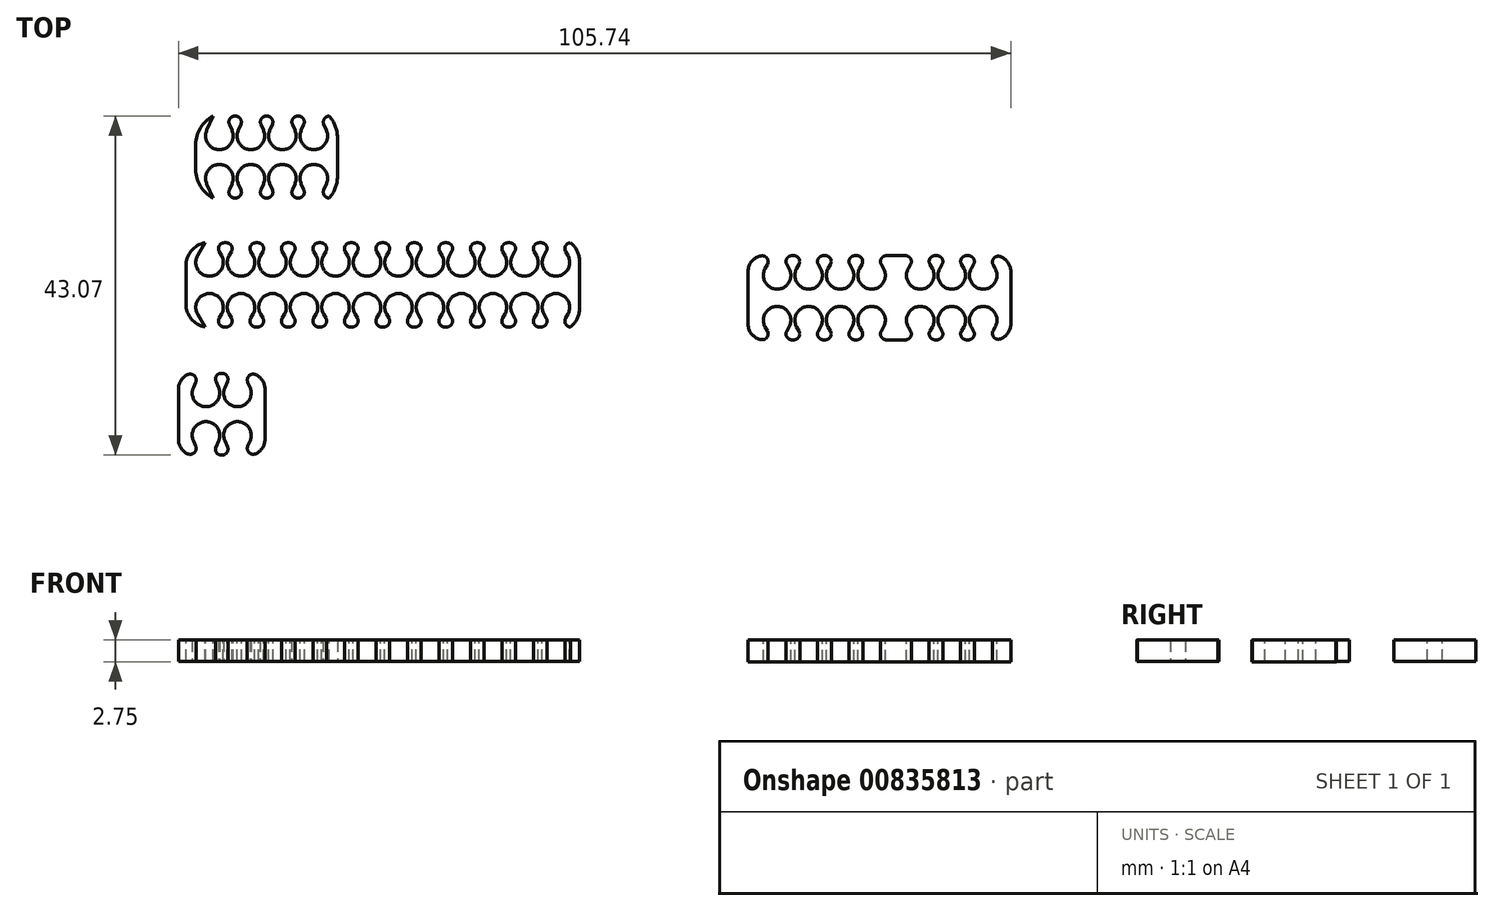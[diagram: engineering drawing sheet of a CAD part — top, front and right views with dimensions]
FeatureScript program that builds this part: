
annotation { "Feature Type Name" : "Feature", "Feature Type Description" : "" }
export const myFeature = defineFeature(function(context is Context, id is Id, definition is map)
    precondition{}
    {
        {
            var Q0;
            Q0=qCreatedBy(makeId("Top.planeOp"),FACE);
            var sketch = newSketch(context, id + "F0", { "sketchPlane" : qUnion([Q0])});
            skLineSegment(sketch, "E0.bottom", {"start": v(-25, 10.7) * mm, "end": v(25, 10.7) * mm});
            skLineSegment(sketch, "E0.top", {"start": v(-25, 0) * mm, "end": v(25, 0) * mm});
            skLineSegment(sketch, "E0.left", {"start": v(-25, 10.7) * mm, "end": v(-25, 0) * mm});
            skLineSegment(sketch, "E0.right", {"start": v(25, 10.7) * mm, "end": v(25, 0) * mm});
            skSolve(sketch);
        }
        {
            var Q0;
            Q0=makeQuery(id+"F0.imprint","IMPRINT",FACE,{"disambiguationData":[TD([[makeQuery(id+"F0.imprint","IMPRINT",EDGE,{"derivedFrom":sQuery(id+"F0.wireOp",EDGE,"E0.bottom")}),-1.0]])]});
            extrude(context, id + "F1", {"entities" : qUnion([Q0]), "depth" : 2.7 * mm});
        }
        {
            var Q0;
            Q0=makeQuery(id+"F1.opExtrude","CAP_FACE",FACE,{"disambiguationData":[OSD([sQuery(id+"F0.wireOp",EDGE,"E0.bottom"),sQuery(id+"F0.wireOp",EDGE,"E0.top"),sQuery(id+"F0.wireOp",EDGE,"E0.left"),sQuery(id+"F0.wireOp",EDGE,"E0.right")])],"isStart":false});
            var sketch = newSketch(context, id + "F2", { "sketchPlane" : qUnion([Q0])});
            skArc(sketch, "E1", {"start": v(-23.52, 9.07) * mm, "mid": v(-22, 6.45) * mm, "end": v(-20.48, 9.07) * mm});
            skArc(sketch, "E2", {"start": v(-19.52, 9.07) * mm, "mid": v(-18, 6.45) * mm, "end": v(-16.48, 9.07) * mm});
            skArc(sketch, "E3", {"start": v(-15.52, 9.07) * mm, "mid": v(-14, 6.45) * mm, "end": v(-12.48, 9.07) * mm});
            skArc(sketch, "E4", {"start": v(-11.52, 9.07) * mm, "mid": v(-10, 6.45) * mm, "end": v(-8.48, 9.07) * mm});
            skArc(sketch, "E5", {"start": v(-7.52, 9.07) * mm, "mid": v(-6, 6.45) * mm, "end": v(-4.48, 9.07) * mm});
            skArc(sketch, "E6", {"start": v(-3.52, 9.07) * mm, "mid": v(-2, 6.45) * mm, "end": v(-0.48, 9.07) * mm});
            skLineSegment(sketch, "E7", {"start": v(-19.52, 9.07) * mm, "end": v(-18.59, 10.7) * mm});
            skLineSegment(sketch, "E8", {"start": v(-16.48, 9.07) * mm, "end": v(-17.41, 10.7) * mm});
            skLineSegment(sketch, "E9", {"start": v(-15.52, 9.07) * mm, "end": v(-14.59, 10.7) * mm});
            skLineSegment(sketch, "E10", {"start": v(-12.48, 9.07) * mm, "end": v(-13.41, 10.7) * mm});
            skLineSegment(sketch, "E11", {"start": v(-11.52, 9.07) * mm, "end": v(-10.59, 10.7) * mm});
            skLineSegment(sketch, "E12", {"start": v(-8.48, 9.07) * mm, "end": v(-9.41, 10.7) * mm});
            skLineSegment(sketch, "E13", {"start": v(-7.52, 9.07) * mm, "end": v(-6.59, 10.7) * mm});
            skLineSegment(sketch, "E14", {"start": v(-4.48, 9.07) * mm, "end": v(-5.41, 10.7) * mm});
            skLineSegment(sketch, "E15", {"start": v(-0.48, 9.07) * mm, "end": v(-1.41, 10.7) * mm});
            skLineSegment(sketch, "E16", {"start": v(-23.52, 9.07) * mm, "end": v(-22.59, 10.7) * mm});
            skLineSegment(sketch, "E17", {"start": v(-18.59, 10.7) * mm, "end": v(-17.41, 10.7) * mm});
            skLineSegment(sketch, "E18", {"start": v(-14.59, 10.7) * mm, "end": v(-13.41, 10.7) * mm});
            skLineSegment(sketch, "E19", {"start": v(-10.59, 10.7) * mm, "end": v(-9.41, 10.7) * mm});
            skLineSegment(sketch, "E20", {"start": v(-6.59, 10.7) * mm, "end": v(-5.41, 10.7) * mm});
            skLineSegment(sketch, "E21", {"start": v(-2.59, 10.7) * mm, "end": v(-1.41, 10.7) * mm});
            skLineSegment(sketch, "E22", {"start": v(-25, 5.35) * mm, "end": v(25, 5.35) * mm});
            skLineSegment(sketch, "E23.MirrorCS", {"start": v(-15.52, 1.63) * mm, "end": v(-14.59, 0) * mm});
            skLineSegment(sketch, "E24.MirrorCS", {"start": v(-8.48, 1.63) * mm, "end": v(-9.41, 0) * mm});
            skLineSegment(sketch, "E25.MirrorCS", {"start": v(-7.52, 1.63) * mm, "end": v(-6.59, 0) * mm});
            skLineSegment(sketch, "E26.MirrorCS", {"start": v(-16.48, 1.63) * mm, "end": v(-17.41, 0) * mm});
            skLineSegment(sketch, "E27.MirrorCS", {"start": v(-4.48, 1.63) * mm, "end": v(-5.41, 0) * mm});
            skArc(sketch, "E28.MirrorCS", {"start": v(-23.52, 1.63) * mm, "mid": v(-22, 4.25) * mm, "end": v(-20.48, 1.63) * mm});
            skArc(sketch, "E29.MirrorCS", {"start": v(-3.52, 1.63) * mm, "mid": v(-2, 4.25) * mm, "end": v(-0.48, 1.63) * mm});
            skLineSegment(sketch, "E30.MirrorCS", {"start": v(-19.52, 1.63) * mm, "end": v(-18.59, 0) * mm});
            skArc(sketch, "E31.MirrorCS", {"start": v(-19.52, 1.63) * mm, "mid": v(-18, 4.25) * mm, "end": v(-16.48, 1.63) * mm});
            skArc(sketch, "E32.MirrorCS", {"start": v(-7.52, 1.63) * mm, "mid": v(-6, 4.25) * mm, "end": v(-4.48, 1.63) * mm});
            skArc(sketch, "E33.MirrorCS", {"start": v(-11.52, 1.63) * mm, "mid": v(-10, 4.25) * mm, "end": v(-8.48, 1.63) * mm});
            skArc(sketch, "E34.MirrorCS", {"start": v(-15.52, 1.63) * mm, "mid": v(-14, 4.25) * mm, "end": v(-12.48, 1.63) * mm});
            skLineSegment(sketch, "E35.MirrorCS", {"start": v(-23.52, 1.63) * mm, "end": v(-22.59, 0) * mm});
            skLineSegment(sketch, "E36.MirrorCS", {"start": v(-2.59, 0) * mm, "end": v(-1.41, 0) * mm});
            skLineSegment(sketch, "E37.MirrorCS", {"start": v(-6.59, 0) * mm, "end": v(-5.41, 0) * mm});
            skLineSegment(sketch, "E38.MirrorCS", {"start": v(-18.59, 0) * mm, "end": v(-17.41, 0) * mm});
            skLineSegment(sketch, "E39.MirrorCS", {"start": v(-11.52, 1.63) * mm, "end": v(-10.59, 0) * mm});
            skLineSegment(sketch, "E40.MirrorCS", {"start": v(-14.59, 0) * mm, "end": v(-13.41, 0) * mm});
            skLineSegment(sketch, "E41.MirrorCS", {"start": v(-10.59, 0) * mm, "end": v(-9.41, 0) * mm});
            skLineSegment(sketch, "E42.MirrorCS", {"start": v(-12.48, 1.63) * mm, "end": v(-13.41, 0) * mm});
            skLineSegment(sketch, "E43.MirrorCS", {"start": v(-0.48, 1.63) * mm, "end": v(-1.41, 0) * mm});
            skLineSegment(sketch, "E44", {"start": v(-3.52, 9.07) * mm, "end": v(-2.59, 10.7) * mm});
            skLineSegment(sketch, "E45", {"start": v(-3.52, 1.63) * mm, "end": v(-2.59, 0) * mm});
            skLineSegment(sketch, "E46", {"start": v(-20.48, 9.07) * mm, "end": v(-21.41, 10.7) * mm});
            skLineSegment(sketch, "E47", {"start": v(-21.41, 10.7) * mm, "end": v(-22.59, 10.7) * mm});
            skLineSegment(sketch, "E48", {"start": v(-20.48, 1.63) * mm, "end": v(-21.41, 0) * mm});
            skLineSegment(sketch, "E49", {"start": v(-21.41, 0) * mm, "end": v(-22.59, 0) * mm});
            skLineSegment(sketch, "E50.MirrorCS", {"start": v(6.59, 0) * mm, "end": v(5.41, 0) * mm});
            skLineSegment(sketch, "E51.MirrorCS", {"start": v(21.41, 0) * mm, "end": v(22.59, 0) * mm});
            skLineSegment(sketch, "E52.MirrorCS", {"start": v(10.59, 10.7) * mm, "end": v(9.41, 10.7) * mm});
            skLineSegment(sketch, "E53.MirrorCS", {"start": v(6.59, 10.7) * mm, "end": v(5.41, 10.7) * mm});
            skLineSegment(sketch, "E54.MirrorCS", {"start": v(21.41, 10.7) * mm, "end": v(22.59, 10.7) * mm});
            skLineSegment(sketch, "E55.MirrorCS", {"start": v(18.59, 10.7) * mm, "end": v(17.41, 10.7) * mm});
            skLineSegment(sketch, "E56.MirrorCS", {"start": v(2.59, 0) * mm, "end": v(1.41, 0) * mm});
            skLineSegment(sketch, "E57.MirrorCS", {"start": v(18.59, 0) * mm, "end": v(17.41, 0) * mm});
            skLineSegment(sketch, "E58.MirrorCS", {"start": v(2.59, 10.7) * mm, "end": v(1.41, 10.7) * mm});
            skLineSegment(sketch, "E59.MirrorCS", {"start": v(10.59, 0) * mm, "end": v(9.41, 0) * mm});
            skLineSegment(sketch, "E60.MirrorCS", {"start": v(14.59, 10.7) * mm, "end": v(13.41, 10.7) * mm});
            skLineSegment(sketch, "E61.MirrorCS", {"start": v(14.59, 0) * mm, "end": v(13.41, 0) * mm});
            skArc(sketch, "E62.MirrorCS", {"start": v(11.52, 9.07) * mm, "mid": v(10, 6.45) * mm, "end": v(8.48, 9.07) * mm});
            skLineSegment(sketch, "E63.MirrorCS", {"start": v(15.52, 1.63) * mm, "end": v(14.59, 0) * mm});
            skArc(sketch, "E64.MirrorCS", {"start": v(15.52, 1.63) * mm, "mid": v(14, 4.25) * mm, "end": v(12.48, 1.63) * mm});
            skLineSegment(sketch, "E65.MirrorCS", {"start": v(4.48, 1.63) * mm, "end": v(5.41, 0) * mm});
            skArc(sketch, "E66.MirrorCS", {"start": v(3.52, 1.63) * mm, "mid": v(2, 4.25) * mm, "end": v(0.48, 1.63) * mm});
            skArc(sketch, "E67.MirrorCS", {"start": v(3.52, 9.07) * mm, "mid": v(2, 6.45) * mm, "end": v(0.48, 9.07) * mm});
            skLineSegment(sketch, "E68.MirrorCS", {"start": v(15.52, 9.07) * mm, "end": v(14.59, 10.7) * mm});
            skLineSegment(sketch, "E69.MirrorCS", {"start": v(12.48, 9.07) * mm, "end": v(13.41, 10.7) * mm});
            skLineSegment(sketch, "E70.MirrorCS", {"start": v(16.48, 9.07) * mm, "end": v(17.41, 10.7) * mm});
            skLineSegment(sketch, "E71.MirrorCS", {"start": v(23.52, 9.07) * mm, "end": v(22.59, 10.7) * mm});
            skArc(sketch, "E72.MirrorCS", {"start": v(7.52, 9.07) * mm, "mid": v(6, 6.45) * mm, "end": v(4.48, 9.07) * mm});
            skLineSegment(sketch, "E73.MirrorCS", {"start": v(25, 5.35) * mm, "end": v(-25, 5.35) * mm});
            skLineSegment(sketch, "E74.MirrorCS", {"start": v(7.52, 1.63) * mm, "end": v(6.59, 0) * mm});
            skArc(sketch, "E75.MirrorCS", {"start": v(19.52, 9.07) * mm, "mid": v(18, 6.45) * mm, "end": v(16.48, 9.07) * mm});
            skLineSegment(sketch, "E76.MirrorCS", {"start": v(3.52, 1.63) * mm, "end": v(2.59, 0) * mm});
            skLineSegment(sketch, "E77.MirrorCS", {"start": v(19.52, 1.63) * mm, "end": v(18.59, 0) * mm});
            skLineSegment(sketch, "E78.MirrorCS", {"start": v(23.52, 1.63) * mm, "end": v(22.59, 0) * mm});
            skArc(sketch, "E79.MirrorCS", {"start": v(15.52, 9.07) * mm, "mid": v(14, 6.45) * mm, "end": v(12.48, 9.07) * mm});
            skArc(sketch, "E80.MirrorCS", {"start": v(11.52, 1.63) * mm, "mid": v(10, 4.25) * mm, "end": v(8.48, 1.63) * mm});
            skArc(sketch, "E81.MirrorCS", {"start": v(7.52, 1.63) * mm, "mid": v(6, 4.25) * mm, "end": v(4.48, 1.63) * mm});
            skLineSegment(sketch, "E82.MirrorCS", {"start": v(12.48, 1.63) * mm, "end": v(13.41, 0) * mm});
            skLineSegment(sketch, "E83.MirrorCS", {"start": v(8.48, 9.07) * mm, "end": v(9.41, 10.7) * mm});
            skArc(sketch, "E84.MirrorCS", {"start": v(23.52, 9.07) * mm, "mid": v(22, 6.45) * mm, "end": v(20.48, 9.07) * mm});
            skLineSegment(sketch, "E85.MirrorCS", {"start": v(20.48, 9.07) * mm, "end": v(21.41, 10.7) * mm});
            skLineSegment(sketch, "E86.MirrorCS", {"start": v(7.52, 9.07) * mm, "end": v(6.59, 10.7) * mm});
            skLineSegment(sketch, "E87.MirrorCS", {"start": v(0.48, 1.63) * mm, "end": v(1.41, 0) * mm});
            skLineSegment(sketch, "E88.MirrorCS", {"start": v(16.48, 1.63) * mm, "end": v(17.41, 0) * mm});
            skLineSegment(sketch, "E89.MirrorCS", {"start": v(20.48, 1.63) * mm, "end": v(21.41, 0) * mm});
            skLineSegment(sketch, "E90.MirrorCS", {"start": v(11.52, 1.63) * mm, "end": v(10.59, 0) * mm});
            skLineSegment(sketch, "E91.MirrorCS", {"start": v(11.52, 9.07) * mm, "end": v(10.59, 10.7) * mm});
            skArc(sketch, "E92.MirrorCS", {"start": v(23.52, 1.63) * mm, "mid": v(22, 4.25) * mm, "end": v(20.48, 1.63) * mm});
            skLineSegment(sketch, "E93.MirrorCS", {"start": v(3.52, 9.07) * mm, "end": v(2.59, 10.7) * mm});
            skArc(sketch, "E94.MirrorCS", {"start": v(19.52, 1.63) * mm, "mid": v(18, 4.25) * mm, "end": v(16.48, 1.63) * mm});
            skLineSegment(sketch, "E95.MirrorCS", {"start": v(4.48, 9.07) * mm, "end": v(5.41, 10.7) * mm});
            skLineSegment(sketch, "E96.MirrorCS", {"start": v(19.52, 9.07) * mm, "end": v(18.59, 10.7) * mm});
            skLineSegment(sketch, "E97.MirrorCS", {"start": v(8.48, 1.63) * mm, "end": v(9.41, 0) * mm});
            skLineSegment(sketch, "E98.MirrorCS", {"start": v(0.48, 9.07) * mm, "end": v(1.41, 10.7) * mm});
            skArc(sketch, "E99", {"start": v(48.58, 7.43) * mm, "mid": v(50.1, 4.82) * mm, "end": v(51.62, 7.43) * mm});
            skLineSegment(sketch, "E100", {"start": v(51.62, 7.43) * mm, "end": v(50.69, 9.07) * mm});
            skArc(sketch, "E101.MirrorCS", {"start": v(48.58, 0) * mm, "mid": v(50.1, 2.62) * mm, "end": v(51.62, 0) * mm});
            skLineSegment(sketch, "E102.MirrorCS", {"start": v(51.62, 0) * mm, "end": v(50.69, -1.63) * mm});
            skLineSegment(sketch, "E103", {"start": v(48.58, 7.43) * mm, "end": v(49.51, 9.07) * mm});
            skLineSegment(sketch, "E104", {"start": v(48.58, 0) * mm, "end": v(49.51, -1.63) * mm});
            skArc(sketch, "E105.MirrorCS", {"start": v(63.62, 7.43) * mm, "mid": v(62.1, 4.82) * mm, "end": v(60.58, 7.43) * mm});
            skLineSegment(sketch, "E106.MirrorCS", {"start": v(56.58, 0) * mm, "end": v(57.51, -1.63) * mm});
            skArc(sketch, "E107.MirrorCS", {"start": v(55.62, 0) * mm, "mid": v(54.1, 2.62) * mm, "end": v(52.58, 0) * mm});
            skArc(sketch, "E108.MirrorCS", {"start": v(55.62, 7.43) * mm, "mid": v(54.1, 4.82) * mm, "end": v(52.58, 7.43) * mm});
            skArc(sketch, "E109.MirrorCS", {"start": v(59.62, 7.43) * mm, "mid": v(58.1, 4.82) * mm, "end": v(56.58, 7.43) * mm});
            skLineSegment(sketch, "E110.MirrorCS", {"start": v(59.62, 0) * mm, "end": v(58.69, -1.63) * mm});
            skLineSegment(sketch, "E111.MirrorCS", {"start": v(55.62, 0) * mm, "end": v(54.69, -1.63) * mm});
            skArc(sketch, "E112.MirrorCS", {"start": v(63.62, 0) * mm, "mid": v(62.1, 2.62) * mm, "end": v(60.58, 0) * mm});
            skArc(sketch, "E113.MirrorCS", {"start": v(59.62, 0) * mm, "mid": v(58.1, 2.62) * mm, "end": v(56.58, 0) * mm});
            skLineSegment(sketch, "E114.MirrorCS", {"start": v(60.58, 7.43) * mm, "end": v(61.51, 9.07) * mm});
            skLineSegment(sketch, "E115.MirrorCS", {"start": v(59.62, 7.43) * mm, "end": v(58.69, 9.07) * mm});
            skLineSegment(sketch, "E116.MirrorCS", {"start": v(52.58, 0) * mm, "end": v(53.51, -1.63) * mm});
            skLineSegment(sketch, "E117.MirrorCS", {"start": v(63.62, 0) * mm, "end": v(62.69, -1.63) * mm});
            skLineSegment(sketch, "E118.MirrorCS", {"start": v(63.62, 7.43) * mm, "end": v(62.69, 9.07) * mm});
            skLineSegment(sketch, "E119.MirrorCS", {"start": v(55.62, 7.43) * mm, "end": v(54.69, 9.07) * mm});
            skLineSegment(sketch, "E120.MirrorCS", {"start": v(56.58, 7.43) * mm, "end": v(57.51, 9.07) * mm});
            skLineSegment(sketch, "E121.MirrorCS", {"start": v(60.58, 0) * mm, "end": v(61.51, -1.63) * mm});
            skLineSegment(sketch, "E122.MirrorCS", {"start": v(52.58, 7.43) * mm, "end": v(53.51, 9.07) * mm});
            skPoint(sketch, "E123.firstSnap0", {"position": v(50.1, 9.07) * mm});
            skLineSegment(sketch, "E123.bottom", {"start": v(46.4, 9.07) * mm, "end": v(49.51, 9.07) * mm});
            skLineSegment(sketch, "E123.top", {"start": v(46.4, -1.63) * mm, "end": v(49.51, -1.63) * mm});
            skLineSegment(sketch, "E123.left", {"start": v(46.4, 9.07) * mm, "end": v(46.4, -1.63) * mm});
            skLineSegment(sketch, "E124.trimOffspring", {"start": v(50.69, -1.63) * mm, "end": v(53.51, -1.63) * mm});
            skLineSegment(sketch, "E125.trimOffspring", {"start": v(54.69, -1.63) * mm, "end": v(57.51, -1.63) * mm});
            skLineSegment(sketch, "E126.trimOffspring", {"start": v(58.69, -1.63) * mm, "end": v(61.51, -1.63) * mm});
            skLineSegment(sketch, "E127.trimOffspring", {"start": v(58.69, 9.07) * mm, "end": v(61.51, 9.07) * mm});
            skLineSegment(sketch, "E128.trimOffspring", {"start": v(54.69, 9.07) * mm, "end": v(57.51, 9.07) * mm});
            skLineSegment(sketch, "E129.trimOffspring", {"start": v(50.69, 9.07) * mm, "end": v(53.51, 9.07) * mm});
            skLineSegment(sketch, "E130", {"start": v(62.69, 9.07) * mm, "end": v(65.32, 9.07) * mm});
            skLineSegment(sketch, "E131", {"start": v(62.69, -1.63) * mm, "end": v(65.32, -1.63) * mm});
            skLineSegment(sketch, "E132.MirrorCS", {"start": v(75.69, 9.07) * mm, "end": v(72.87, 9.07) * mm});
            skLineSegment(sketch, "E133.MirrorCS", {"start": v(69.8, 7.43) * mm, "end": v(68.87, 9.07) * mm});
            skLineSegment(sketch, "E134.MirrorCS", {"start": v(70.76, 0) * mm, "end": v(71.69, -1.63) * mm});
            skLineSegment(sketch, "E135.MirrorCS", {"start": v(70.76, 7.43) * mm, "end": v(71.69, 9.07) * mm});
            skLineSegment(sketch, "E136.MirrorCS", {"start": v(75.69, -1.63) * mm, "end": v(72.87, -1.63) * mm});
            skLineSegment(sketch, "E137.MirrorCS", {"start": v(71.69, 9.07) * mm, "end": v(68.87, 9.07) * mm});
            skArc(sketch, "E138.MirrorCS", {"start": v(66.76, 0) * mm, "mid": v(68.28, 2.62) * mm, "end": v(69.8, 0) * mm});
            skArc(sketch, "E139.MirrorCS", {"start": v(70.76, 0) * mm, "mid": v(72.28, 2.62) * mm, "end": v(73.8, 0) * mm});
            skArc(sketch, "E140.MirrorCS", {"start": v(74.76, 7.43) * mm, "mid": v(76.28, 4.82) * mm, "end": v(77.8, 7.43) * mm});
            skArc(sketch, "E141.MirrorCS", {"start": v(70.76, 7.43) * mm, "mid": v(72.28, 4.82) * mm, "end": v(73.8, 7.43) * mm});
            skLineSegment(sketch, "E142.MirrorCS", {"start": v(77.8, 7.43) * mm, "end": v(76.87, 9.07) * mm});
            skLineSegment(sketch, "E143.MirrorCS", {"start": v(73.8, 0) * mm, "end": v(72.87, -1.63) * mm});
            skLineSegment(sketch, "E144.MirrorCS", {"start": v(69.8, 0) * mm, "end": v(68.87, -1.63) * mm});
            skLineSegment(sketch, "E145.MirrorCS", {"start": v(66.76, 7.43) * mm, "end": v(67.69, 9.07) * mm});
            skLineSegment(sketch, "E146.MirrorCS", {"start": v(71.69, -1.63) * mm, "end": v(68.87, -1.63) * mm});
            skLineSegment(sketch, "E147.MirrorCS", {"start": v(77.8, 0) * mm, "end": v(76.87, -1.63) * mm});
            skArc(sketch, "E148.MirrorCS", {"start": v(74.76, 0) * mm, "mid": v(76.28, 2.62) * mm, "end": v(77.8, 0) * mm});
            skArc(sketch, "E149.MirrorCS", {"start": v(66.76, 7.43) * mm, "mid": v(68.28, 4.82) * mm, "end": v(69.8, 7.43) * mm});
            skLineSegment(sketch, "E150.MirrorCS", {"start": v(73.8, 7.43) * mm, "end": v(72.87, 9.07) * mm});
            skLineSegment(sketch, "E151.MirrorCS", {"start": v(74.76, 7.43) * mm, "end": v(75.69, 9.07) * mm});
            skLineSegment(sketch, "E152.MirrorCS", {"start": v(66.76, 0) * mm, "end": v(67.69, -1.63) * mm});
            skLineSegment(sketch, "E153.MirrorCS", {"start": v(74.76, 0) * mm, "end": v(75.69, -1.63) * mm});
            skLineSegment(sketch, "E154", {"start": v(65.32, 9.07) * mm, "end": v(67.69, 9.07) * mm});
            skLineSegment(sketch, "E155", {"start": v(65.32, -1.63) * mm, "end": v(67.69, -1.63) * mm});
            skLineSegment(sketch, "E156", {"start": v(79.78, 9.07) * mm, "end": v(79.78, -1.63) * mm});
            skLineSegment(sketch, "E157", {"start": v(79.78, -1.63) * mm, "end": v(76.87, -1.63) * mm});
            skLineSegment(sketch, "E158", {"start": v(76.87, 9.07) * mm, "end": v(79.78, 9.07) * mm});
            skSolve(sketch);
        }
        {
            var Q0;
            Q0=qSketchRegion(id+"F2",true);
            extrude(context, id + "F3", {"entities" : qUnion([Q0]), "operationType" : NewBodyOperationType.REMOVE, "oppositeDirection" : true, "depth" : 25 * mm});
        }
        {
            var Q0;
            Q0=makeQuery(id+"F3.boolean.opBoolean","COPY",EDGE,{"derivedFrom":makeQuery(id+"F3.opExtrude","SWEPT_EDGE",EDGE,{"disambiguationData":[OSD([sQuery(id+"F0.wireOp",EDGE,"E0.top"),sQuery(id+"F2.wireOp",EDGE,"E244.MirrorCS"),sQuery(id+"F2.wireOp",EDGE,"E248.MirrorCS")])]})});
            var Q1;
            Q1=makeQuery(id+"F3.boolean.opBoolean","COPY",EDGE,{"derivedFrom":makeQuery(id+"F3.opExtrude","SWEPT_EDGE",EDGE,{"disambiguationData":[OSD([sQuery(id+"F0.wireOp",EDGE,"E0.top"),sQuery(id+"F2.wireOp",EDGE,"E247.MirrorCS"),sQuery(id+"F2.wireOp",EDGE,"E248.MirrorCS")])]})});
            var Q2;
            Q2=makeQuery(id+"F3.boolean.opBoolean","COPY",EDGE,{"derivedFrom":makeQuery(id+"F3.opExtrude","SWEPT_EDGE",EDGE,{"disambiguationData":[OSD([sQuery(id+"F0.wireOp",EDGE,"E0.bottom"),sQuery(id+"F2.wireOp",EDGE,"IQOr8gKH-AA3r-RsNy-xa8J-JxTkXKXGDwke"),sQuery(id+"F2.wireOp",EDGE,"qSGI12MA-lLNW-cEYR-Ucfo-gfGJAkbjLQMW")])]})});
            var Q3;
            Q3=makeQuery(id+"F3.boolean.opBoolean","COPY",EDGE,{"derivedFrom":makeQuery(id+"F3.opExtrude","SWEPT_EDGE",EDGE,{"disambiguationData":[OSD([sQuery(id+"F0.wireOp",EDGE,"E0.top"),sQuery(id+"F2.wireOp",EDGE,"E36.MirrorCS"),sQuery(id+"F2.wireOp",EDGE,"E43.MirrorCS")])]})});
            var Q4;
            Q4=makeQuery(id+"F3.boolean.opBoolean","COPY",EDGE,{"derivedFrom":makeQuery(id+"F3.opExtrude","SWEPT_EDGE",EDGE,{"disambiguationData":[OSD([sQuery(id+"F0.wireOp",EDGE,"E0.top"),sQuery(id+"F2.wireOp",EDGE,"E243.MirrorCS"),sQuery(id+"F2.wireOp",EDGE,"E36.MirrorCS")])]})});
            var Q5;
            Q5=makeQuery(id+"F3.boolean.opBoolean","COPY",EDGE,{"derivedFrom":makeQuery(id+"F3.opExtrude","SWEPT_EDGE",EDGE,{"disambiguationData":[OSD([sQuery(id+"F0.wireOp",EDGE,"E0.top"),sQuery(id+"F2.wireOp",EDGE,"E27.MirrorCS"),sQuery(id+"F2.wireOp",EDGE,"E37.MirrorCS")])]})});
            var Q6;
            Q6=makeQuery(id+"F3.boolean.opBoolean","COPY",EDGE,{"derivedFrom":makeQuery(id+"F3.opExtrude","SWEPT_EDGE",EDGE,{"disambiguationData":[OSD([sQuery(id+"F0.wireOp",EDGE,"E0.top"),sQuery(id+"F2.wireOp",EDGE,"E25.MirrorCS"),sQuery(id+"F2.wireOp",EDGE,"E37.MirrorCS")])]})});
            var Q7;
            Q7=makeQuery(id+"F3.boolean.opBoolean","COPY",EDGE,{"derivedFrom":makeQuery(id+"F3.opExtrude","SWEPT_EDGE",EDGE,{"disambiguationData":[OSD([sQuery(id+"F0.wireOp",EDGE,"E0.top"),sQuery(id+"F2.wireOp",EDGE,"E24.MirrorCS"),sQuery(id+"F2.wireOp",EDGE,"E41.MirrorCS")])]})});
            var Q8;
            Q8=makeQuery(id+"F3.boolean.opBoolean","COPY",EDGE,{"derivedFrom":makeQuery(id+"F3.opExtrude","SWEPT_EDGE",EDGE,{"disambiguationData":[OSD([sQuery(id+"F0.wireOp",EDGE,"E0.top"),sQuery(id+"F2.wireOp",EDGE,"E39.MirrorCS"),sQuery(id+"F2.wireOp",EDGE,"E41.MirrorCS")])]})});
            var Q9;
            Q9=makeQuery(id+"F3.boolean.opBoolean","COPY",EDGE,{"derivedFrom":makeQuery(id+"F3.opExtrude","SWEPT_EDGE",EDGE,{"disambiguationData":[OSD([sQuery(id+"F0.wireOp",EDGE,"E0.top"),sQuery(id+"F2.wireOp",EDGE,"E40.MirrorCS"),sQuery(id+"F2.wireOp",EDGE,"E42.MirrorCS")])]})});
            var Q10;
            Q10=makeQuery(id+"F3.boolean.opBoolean","COPY",EDGE,{"derivedFrom":makeQuery(id+"F3.opExtrude","SWEPT_EDGE",EDGE,{"disambiguationData":[OSD([sQuery(id+"F0.wireOp",EDGE,"E0.top"),sQuery(id+"F2.wireOp",EDGE,"E23.MirrorCS"),sQuery(id+"F2.wireOp",EDGE,"E40.MirrorCS")])]})});
            var Q11;
            Q11=makeQuery(id+"F3.boolean.opBoolean","COPY",EDGE,{"derivedFrom":makeQuery(id+"F3.opExtrude","SWEPT_EDGE",EDGE,{"disambiguationData":[OSD([sQuery(id+"F0.wireOp",EDGE,"E0.top"),sQuery(id+"F2.wireOp",EDGE,"E26.MirrorCS"),sQuery(id+"F2.wireOp",EDGE,"E38.MirrorCS")])]})});
            var Q12;
            Q12=makeQuery(id+"F3.boolean.opBoolean","COPY",EDGE,{"derivedFrom":makeQuery(id+"F3.opExtrude","SWEPT_EDGE",EDGE,{"disambiguationData":[OSD([sQuery(id+"F0.wireOp",EDGE,"E0.top"),sQuery(id+"F2.wireOp",EDGE,"E30.MirrorCS"),sQuery(id+"F2.wireOp",EDGE,"E38.MirrorCS")])]})});
            var Q13;
            Q13=makeQuery(id+"F3.boolean.opBoolean","COPY",EDGE,{"derivedFrom":makeQuery(id+"F3.opExtrude","SWEPT_EDGE",EDGE,{"disambiguationData":[OSD([sQuery(id+"F0.wireOp",EDGE,"E0.top"),sQuery(id+"F2.wireOp",EDGE,"E254.MirrorCS"),sQuery(id+"F2.wireOp",EDGE,"E255.MirrorCS")])]})});
            var Q14;
            Q14=makeQuery(id+"F3.boolean.opBoolean","COPY",EDGE,{"derivedFrom":makeQuery(id+"F3.opExtrude","SWEPT_EDGE",EDGE,{"disambiguationData":[OSD([sQuery(id+"F0.wireOp",EDGE,"E0.top"),sQuery(id+"F2.wireOp",EDGE,"E35.MirrorCS"),sQuery(id+"F2.wireOp",EDGE,"E254.MirrorCS")])]})});
            var Q15;
            Q15=makeQuery(id+"F3.boolean.opBoolean","COPY",EDGE,{"derivedFrom":makeQuery(id+"F3.opExtrude","SWEPT_EDGE",EDGE,{"disambiguationData":[OSD([sQuery(id+"F0.wireOp",EDGE,"E0.bottom"),sQuery(id+"F2.wireOp",EDGE,"UjLKNyOy-sdcN-vUJI-xe36-BtCcAArnIZbs"),sQuery(id+"F2.wireOp",EDGE,"qSGI12MA-lLNW-cEYR-Ucfo-gfGJAkbjLQMW")])]})});
            var Q16;
            Q16=makeQuery(id+"F3.boolean.opBoolean","COPY",EDGE,{"derivedFrom":makeQuery(id+"F3.opExtrude","SWEPT_EDGE",EDGE,{"disambiguationData":[OSD([sQuery(id+"F0.wireOp",EDGE,"E0.bottom"),sQuery(id+"F2.wireOp",EDGE,"E15"),sQuery(id+"F2.wireOp",EDGE,"E21")])]})});
            var Q17;
            Q17=makeQuery(id+"F3.boolean.opBoolean","COPY",EDGE,{"derivedFrom":makeQuery(id+"F3.opExtrude","SWEPT_EDGE",EDGE,{"disambiguationData":[OSD([sQuery(id+"F0.wireOp",EDGE,"E0.bottom"),sQuery(id+"F2.wireOp",EDGE,"1lPn1qKL-qkZ3-ByxJ-MAWl-Qf6jtQHj3nnD"),sQuery(id+"F2.wireOp",EDGE,"E21")])]})});
            var Q18;
            Q18=makeQuery(id+"F3.boolean.opBoolean","COPY",EDGE,{"derivedFrom":makeQuery(id+"F3.opExtrude","SWEPT_EDGE",EDGE,{"disambiguationData":[OSD([sQuery(id+"F0.wireOp",EDGE,"E0.bottom"),sQuery(id+"F2.wireOp",EDGE,"E14"),sQuery(id+"F2.wireOp",EDGE,"E20")])]})});
            var Q19;
            Q19=makeQuery(id+"F3.boolean.opBoolean","COPY",EDGE,{"derivedFrom":makeQuery(id+"F3.opExtrude","SWEPT_EDGE",EDGE,{"disambiguationData":[OSD([sQuery(id+"F0.wireOp",EDGE,"E0.bottom"),sQuery(id+"F2.wireOp",EDGE,"E13"),sQuery(id+"F2.wireOp",EDGE,"E20")])]})});
            var Q20;
            Q20=makeQuery(id+"F3.boolean.opBoolean","COPY",EDGE,{"derivedFrom":makeQuery(id+"F3.opExtrude","SWEPT_EDGE",EDGE,{"disambiguationData":[OSD([sQuery(id+"F0.wireOp",EDGE,"E0.bottom"),sQuery(id+"F2.wireOp",EDGE,"E12"),sQuery(id+"F2.wireOp",EDGE,"E19")])]})});
            var Q21;
            Q21=makeQuery(id+"F3.boolean.opBoolean","COPY",EDGE,{"derivedFrom":makeQuery(id+"F3.opExtrude","SWEPT_EDGE",EDGE,{"disambiguationData":[OSD([sQuery(id+"F0.wireOp",EDGE,"E0.bottom"),sQuery(id+"F2.wireOp",EDGE,"E10"),sQuery(id+"F2.wireOp",EDGE,"E18")])]})});
            var Q22;
            Q22=makeQuery(id+"F3.boolean.opBoolean","COPY",EDGE,{"derivedFrom":makeQuery(id+"F3.opExtrude","SWEPT_EDGE",EDGE,{"disambiguationData":[OSD([sQuery(id+"F0.wireOp",EDGE,"E0.bottom"),sQuery(id+"F2.wireOp",EDGE,"E9"),sQuery(id+"F2.wireOp",EDGE,"E18")])]})});
            var Q23;
            Q23=makeQuery(id+"F3.boolean.opBoolean","COPY",EDGE,{"derivedFrom":makeQuery(id+"F3.opExtrude","SWEPT_EDGE",EDGE,{"disambiguationData":[OSD([sQuery(id+"F0.wireOp",EDGE,"E0.bottom"),sQuery(id+"F2.wireOp",EDGE,"E8"),sQuery(id+"F2.wireOp",EDGE,"E17")])]})});
            var Q24;
            Q24=makeQuery(id+"F3.boolean.opBoolean","COPY",EDGE,{"derivedFrom":makeQuery(id+"F3.opExtrude","SWEPT_EDGE",EDGE,{"disambiguationData":[OSD([sQuery(id+"F0.wireOp",EDGE,"E0.bottom"),sQuery(id+"F2.wireOp",EDGE,"E7"),sQuery(id+"F2.wireOp",EDGE,"E17")])]})});
            var Q25;
            Q25=makeQuery(id+"F3.boolean.opBoolean","COPY",EDGE,{"derivedFrom":makeQuery(id+"F3.opExtrude","SWEPT_EDGE",EDGE,{"disambiguationData":[OSD([sQuery(id+"F0.wireOp",EDGE,"E0.bottom"),sQuery(id+"F2.wireOp",EDGE,"b1TfKxvo-d6YO-5rsT-L5gf-Kxo1XV25pjbY"),sQuery(id+"F2.wireOp",EDGE,"8bgCysRb-rjLR-dHsJ-Bppl-TsGBnFBbDExs")])]})});
            var Q26;
            Q26=makeQuery(id+"F3.boolean.opBoolean","COPY",EDGE,{"derivedFrom":makeQuery(id+"F3.opExtrude","SWEPT_EDGE",EDGE,{"disambiguationData":[OSD([sQuery(id+"F0.wireOp",EDGE,"E0.bottom"),sQuery(id+"F2.wireOp",EDGE,"E16"),sQuery(id+"F2.wireOp",EDGE,"8bgCysRb-rjLR-dHsJ-Bppl-TsGBnFBbDExs")])]})});
            var Q27;
            Q27=makeQuery(id+"F3.boolean.opBoolean","COPY",EDGE,{"derivedFrom":makeQuery(id+"F3.opExtrude","SWEPT_EDGE",EDGE,{"disambiguationData":[OSD([sQuery(id+"F0.wireOp",EDGE,"E0.bottom"),sQuery(id+"F2.wireOp",EDGE,"E11"),sQuery(id+"F2.wireOp",EDGE,"E19")])]})});
            fillet(context, id + "F4", {"entities" : qUnion([Q0, Q1, Q2, Q3, Q4, Q5, Q6, Q7, Q8, Q9, Q10, Q11, Q12, Q13, Q14, Q15, Q16, Q17, Q18, Q19, Q20, Q21, Q22, Q23, Q24, Q25, Q26, Q27]), "radius" : .75 * mm, "tangentPropagation" : true, "allowEdgeOverflow" : false});
        }
        {
            var Q0;
            Q0=makeQuery(id+"F1.opExtrude","SWEPT_EDGE",EDGE,{"disambiguationData":[OSD([sQuery(id+"F0.wireOp",EDGE,"E0.bottom"),sQuery(id+"F0.wireOp",EDGE,"E0.left")])]});
            var Q1;
            Q1=makeQuery(id+"F1.opExtrude","SWEPT_EDGE",EDGE,{"disambiguationData":[OSD([sQuery(id+"F0.wireOp",EDGE,"E0.top"),sQuery(id+"F0.wireOp",EDGE,"E0.left")])]});
            var Q2;
            Q2=makeQuery(id+"F1.opExtrude","SWEPT_EDGE",EDGE,{"disambiguationData":[OSD([sQuery(id+"F0.wireOp",EDGE,"E0.top"),sQuery(id+"F0.wireOp",EDGE,"E0.right")])]});
            var Q3;
            Q3=makeQuery(id+"F1.opExtrude","SWEPT_EDGE",EDGE,{"disambiguationData":[OSD([sQuery(id+"F0.wireOp",EDGE,"E0.bottom"),sQuery(id+"F0.wireOp",EDGE,"E0.right")])]});
            fillet(context, id + "F5", {"entities" : qUnion([Q0, Q1, Q2, Q3]), "radius" : 3 * mm, "tangentPropagation" : true, "allowEdgeOverflow" : false});
        }
        {
            var Q0;
            Q0=qCreatedBy(makeId("Top.planeOp"),FACE);
            var sketch = newSketch(context, id + "F6", { "sketchPlane" : qUnion([Q0])});
            skLineSegment(sketch, "E159.bottom", {"start": v(-23.75, 26.79) * mm, "end": v(-5.75, 26.79) * mm});
            skLineSegment(sketch, "E159.top", {"start": v(-23.75, 16.39) * mm, "end": v(-5.75, 16.39) * mm});
            skLineSegment(sketch, "E159.left", {"start": v(-23.75, 26.79) * mm, "end": v(-23.75, 16.39) * mm});
            skLineSegment(sketch, "E159.right", {"start": v(-5.75, 26.79) * mm, "end": v(-5.75, 16.39) * mm});
            skSolve(sketch);
        }
        {
            var Q0;
            Q0=qSketchRegion(id+"F6",true);
            extrude(context, id + "F7", {"entities" : qUnion([Q0]), "depth" : 2.7 * mm});
        }
        {
            var Q0;
            Q0=makeQuery(id+"F7.opExtrude","CAP_FACE",FACE,{"disambiguationData":[OSD([sQuery(id+"F6.wireOp",EDGE,"E159.bottom"),sQuery(id+"F6.wireOp",EDGE,"E159.top"),sQuery(id+"F6.wireOp",EDGE,"E159.left"),sQuery(id+"F6.wireOp",EDGE,"E159.right")])],"isStart":false});
            var sketch = newSketch(context, id + "F8", { "sketchPlane" : qUnion([Q0])});
            skArc(sketch, "E160", {"start": v(-22.35, 25) * mm, "mid": v(-20.75, 22.54) * mm, "end": v(-19.16, 25) * mm});
            skArc(sketch, "E161", {"start": v(-18.35, 25) * mm, "mid": v(-16.75, 22.54) * mm, "end": v(-15.16, 25) * mm});
            skArc(sketch, "E162", {"start": v(-14.35, 25) * mm, "mid": v(-12.75, 22.54) * mm, "end": v(-11.16, 25) * mm});
            skArc(sketch, "E163", {"start": v(-10.35, 25) * mm, "mid": v(-8.75, 22.54) * mm, "end": v(-7.16, 25) * mm});
            skLineSegment(sketch, "E164", {"start": v(-22.35, 25) * mm, "end": v(-21.54, 26.79) * mm});
            skLineSegment(sketch, "E165", {"start": v(-19.16, 25) * mm, "end": v(-19.96, 26.79) * mm});
            skLineSegment(sketch, "E166", {"start": v(-19.96, 26.79) * mm, "end": v(-21.54, 26.79) * mm});
            skLineSegment(sketch, "E167", {"start": v(-18.35, 25) * mm, "end": v(-17.54, 26.79) * mm});
            skLineSegment(sketch, "E168", {"start": v(-15.16, 25) * mm, "end": v(-15.96, 26.79) * mm});
            skLineSegment(sketch, "E169", {"start": v(-15.96, 26.79) * mm, "end": v(-17.54, 26.79) * mm});
            skLineSegment(sketch, "E170", {"start": v(-14.35, 25) * mm, "end": v(-13.54, 26.79) * mm});
            skLineSegment(sketch, "E171", {"start": v(-11.16, 25) * mm, "end": v(-11.96, 26.79) * mm});
            skLineSegment(sketch, "E172", {"start": v(-11.96, 26.79) * mm, "end": v(-13.54, 26.79) * mm});
            skLineSegment(sketch, "E173", {"start": v(-10.35, 25) * mm, "end": v(-9.54, 26.79) * mm});
            skPoint(sketch, "E173.endSnap0", {"position": v(-12.75, 26.79) * mm});
            skLineSegment(sketch, "E174", {"start": v(-7.16, 25) * mm, "end": v(-7.96, 26.79) * mm});
            skLineSegment(sketch, "E175", {"start": v(-7.96, 26.79) * mm, "end": v(-9.54, 26.79) * mm});
            skLineSegment(sketch, "E176", {"start": v(-23.75, 21.59) * mm, "end": v(-5.75, 21.59) * mm});
            skLineSegment(sketch, "E177.MirrorCS", {"start": v(-11.96, 16.39) * mm, "end": v(-13.54, 16.39) * mm});
            skArc(sketch, "E178.MirrorCS", {"start": v(-10.35, 18.17) * mm, "mid": v(-8.75, 20.64) * mm, "end": v(-7.16, 18.17) * mm});
            skLineSegment(sketch, "E179.MirrorCS", {"start": v(-22.35, 18.17) * mm, "end": v(-21.54, 16.39) * mm});
            skLineSegment(sketch, "E180.MirrorCS", {"start": v(-11.16, 18.17) * mm, "end": v(-11.96, 16.39) * mm});
            skLineSegment(sketch, "E181.MirrorCS", {"start": v(-14.35, 18.17) * mm, "end": v(-13.54, 16.39) * mm});
            skArc(sketch, "E182.MirrorCS", {"start": v(-14.35, 18.17) * mm, "mid": v(-12.75, 20.64) * mm, "end": v(-11.16, 18.17) * mm});
            skLineSegment(sketch, "E183.MirrorCS", {"start": v(-15.96, 16.39) * mm, "end": v(-17.54, 16.39) * mm});
            skLineSegment(sketch, "E184.MirrorCS", {"start": v(-19.16, 18.17) * mm, "end": v(-19.96, 16.39) * mm});
            skPoint(sketch, "E185.MirrorP", {"position": v(-12.75, 16.39) * mm});
            skLineSegment(sketch, "E186.MirrorCS", {"start": v(-19.96, 16.39) * mm, "end": v(-21.54, 16.39) * mm});
            skLineSegment(sketch, "E187.MirrorCS", {"start": v(-15.16, 18.17) * mm, "end": v(-15.96, 16.39) * mm});
            skLineSegment(sketch, "E188.MirrorCS", {"start": v(-18.35, 18.17) * mm, "end": v(-17.54, 16.39) * mm});
            skLineSegment(sketch, "E189.MirrorCS", {"start": v(-10.35, 18.17) * mm, "end": v(-9.54, 16.39) * mm});
            skLineSegment(sketch, "E190.MirrorCS", {"start": v(-7.16, 18.17) * mm, "end": v(-7.96, 16.39) * mm});
            skArc(sketch, "E191.MirrorCS", {"start": v(-18.35, 18.17) * mm, "mid": v(-16.75, 20.64) * mm, "end": v(-15.16, 18.17) * mm});
            skArc(sketch, "E192.MirrorCS", {"start": v(-22.35, 18.17) * mm, "mid": v(-20.75, 20.64) * mm, "end": v(-19.16, 18.17) * mm});
            skLineSegment(sketch, "E193.MirrorCS", {"start": v(-7.96, 16.39) * mm, "end": v(-9.54, 16.39) * mm});
            skArc(sketch, "E194", {"start": v(2.4, 24.68) * mm, "mid": v(3.99, 22.21) * mm, "end": v(5.58, 24.68) * mm});
            skArc(sketch, "E195", {"start": v(6.4, 24.68) * mm, "mid": v(7.99, 22.21) * mm, "end": v(9.58, 24.68) * mm});
            skLineSegment(sketch, "E196", {"start": v(2.4, 24.68) * mm, "end": v(3.2, 26.46) * mm});
            skLineSegment(sketch, "E197", {"start": v(5.58, 24.68) * mm, "end": v(4.78, 26.46) * mm});
            skLineSegment(sketch, "E198", {"start": v(6.4, 24.68) * mm, "end": v(7.2, 26.46) * mm});
            skPoint(sketch, "E198.endSnap0", {"position": v(3.99, 26.46) * mm});
            skLineSegment(sketch, "E199", {"start": v(9.58, 24.68) * mm, "end": v(8.78, 26.46) * mm});
            skArc(sketch, "E200.MirrorCS", {"start": v(6.4, 17.84) * mm, "mid": v(7.99, 20.31) * mm, "end": v(9.58, 17.84) * mm});
            skLineSegment(sketch, "E201.MirrorCS", {"start": v(5.58, 17.84) * mm, "end": v(4.78, 16.06) * mm});
            skLineSegment(sketch, "E202.MirrorCS", {"start": v(2.4, 17.84) * mm, "end": v(3.2, 16.06) * mm});
            skArc(sketch, "E203.MirrorCS", {"start": v(2.4, 17.84) * mm, "mid": v(3.99, 20.31) * mm, "end": v(5.58, 17.84) * mm});
            skPoint(sketch, "E204.MirrorP", {"position": v(3.99, 16.06) * mm});
            skLineSegment(sketch, "E205.MirrorCS", {"start": v(6.4, 17.84) * mm, "end": v(7.2, 16.06) * mm});
            skLineSegment(sketch, "E206.MirrorCS", {"start": v(9.58, 17.84) * mm, "end": v(8.78, 16.06) * mm});
            skLineSegment(sketch, "E207.bottom", {"start": v(0.49, 26.46) * mm, "end": v(3.2, 26.46) * mm});
            skLineSegment(sketch, "E207.top", {"start": v(0.49, 16.06) * mm, "end": v(3.2, 16.06) * mm});
            skLineSegment(sketch, "E207.left", {"start": v(0.49, 26.46) * mm, "end": v(0.49, 16.06) * mm});
            skLineSegment(sketch, "E207.right", {"start": v(11.49, 26.46) * mm, "end": v(11.49, 16.06) * mm});
            skLineSegment(sketch, "E208.trimOffspring", {"start": v(8.78, 26.46) * mm, "end": v(11.49, 26.46) * mm});
            skLineSegment(sketch, "E209.trimOffspring", {"start": v(8.78, 16.06) * mm, "end": v(11.49, 16.06) * mm});
            skLineSegment(sketch, "E210.trimOffspring", {"start": v(4.78, 16.06) * mm, "end": v(7.2, 16.06) * mm});
            skLineSegment(sketch, "E211.trimOffspring", {"start": v(4.78, 26.46) * mm, "end": v(7.2, 26.46) * mm});
            skSolve(sketch);
        }
        {
            var Q0;
            Q0=qSketchRegion(id+"F8",true);
            extrude(context, id + "F9", {"entities" : qUnion([Q0]), "operationType" : NewBodyOperationType.REMOVE, "oppositeDirection" : true, "depth" : 25 * mm});
        }
        {
            var Q0;
            Q0=makeQuery(id+"F9.boolean.opBoolean","COPY",EDGE,{"derivedFrom":makeQuery(id+"F9.opExtrude","SWEPT_EDGE",EDGE,{"disambiguationData":[OSD([sQuery(id+"F6.wireOp",EDGE,"E159.bottom"),sQuery(id+"F8.wireOp",EDGE,"E164"),sQuery(id+"F8.wireOp",EDGE,"E166")])]})});
            var Q1;
            Q1=makeQuery(id+"F9.boolean.opBoolean","COPY",EDGE,{"derivedFrom":makeQuery(id+"F9.opExtrude","SWEPT_EDGE",EDGE,{"disambiguationData":[OSD([sQuery(id+"F6.wireOp",EDGE,"E159.bottom"),sQuery(id+"F8.wireOp",EDGE,"E165"),sQuery(id+"F8.wireOp",EDGE,"E166")])]})});
            var Q2;
            Q2=makeQuery(id+"F9.boolean.opBoolean","COPY",EDGE,{"derivedFrom":makeQuery(id+"F9.opExtrude","SWEPT_EDGE",EDGE,{"disambiguationData":[OSD([sQuery(id+"F6.wireOp",EDGE,"E159.bottom"),sQuery(id+"F8.wireOp",EDGE,"E167"),sQuery(id+"F8.wireOp",EDGE,"E169")])]})});
            var Q3;
            Q3=makeQuery(id+"F9.boolean.opBoolean","COPY",EDGE,{"derivedFrom":makeQuery(id+"F9.opExtrude","SWEPT_EDGE",EDGE,{"disambiguationData":[OSD([sQuery(id+"F6.wireOp",EDGE,"E159.bottom"),sQuery(id+"F8.wireOp",EDGE,"E168"),sQuery(id+"F8.wireOp",EDGE,"E169")])]})});
            var Q4;
            Q4=makeQuery(id+"F9.boolean.opBoolean","COPY",EDGE,{"derivedFrom":makeQuery(id+"F9.opExtrude","SWEPT_EDGE",EDGE,{"disambiguationData":[OSD([sQuery(id+"F6.wireOp",EDGE,"E159.bottom"),sQuery(id+"F8.wireOp",EDGE,"E170"),sQuery(id+"F8.wireOp",EDGE,"E172")])]})});
            var Q5;
            Q5=makeQuery(id+"F9.boolean.opBoolean","COPY",EDGE,{"derivedFrom":makeQuery(id+"F9.opExtrude","SWEPT_EDGE",EDGE,{"disambiguationData":[OSD([sQuery(id+"F6.wireOp",EDGE,"E159.bottom"),sQuery(id+"F8.wireOp",EDGE,"E171"),sQuery(id+"F8.wireOp",EDGE,"E172")])]})});
            var Q6;
            Q6=makeQuery(id+"F9.boolean.opBoolean","COPY",EDGE,{"derivedFrom":makeQuery(id+"F9.opExtrude","SWEPT_EDGE",EDGE,{"disambiguationData":[OSD([sQuery(id+"F6.wireOp",EDGE,"E159.bottom"),sQuery(id+"F8.wireOp",EDGE,"E173"),sQuery(id+"F8.wireOp",EDGE,"E175")])]})});
            var Q7;
            Q7=makeQuery(id+"F9.boolean.opBoolean","COPY",EDGE,{"derivedFrom":makeQuery(id+"F9.opExtrude","SWEPT_EDGE",EDGE,{"disambiguationData":[OSD([sQuery(id+"F6.wireOp",EDGE,"E159.bottom"),sQuery(id+"F8.wireOp",EDGE,"E174"),sQuery(id+"F8.wireOp",EDGE,"E175")])]})});
            var Q8;
            Q8=makeQuery(id+"F9.boolean.opBoolean","COPY",EDGE,{"derivedFrom":makeQuery(id+"F9.opExtrude","SWEPT_EDGE",EDGE,{"disambiguationData":[OSD([sQuery(id+"F6.wireOp",EDGE,"E159.top"),sQuery(id+"F8.wireOp",EDGE,"E179.MirrorCS"),sQuery(id+"F8.wireOp",EDGE,"E186.MirrorCS")])]})});
            var Q9;
            Q9=makeQuery(id+"F9.boolean.opBoolean","COPY",EDGE,{"derivedFrom":makeQuery(id+"F9.opExtrude","SWEPT_EDGE",EDGE,{"disambiguationData":[OSD([sQuery(id+"F6.wireOp",EDGE,"E159.top"),sQuery(id+"F8.wireOp",EDGE,"E183.MirrorCS"),sQuery(id+"F8.wireOp",EDGE,"E188.MirrorCS")])]})});
            var Q10;
            Q10=makeQuery(id+"F9.boolean.opBoolean","COPY",EDGE,{"derivedFrom":makeQuery(id+"F9.opExtrude","SWEPT_EDGE",EDGE,{"disambiguationData":[OSD([sQuery(id+"F6.wireOp",EDGE,"E159.top"),sQuery(id+"F8.wireOp",EDGE,"E184.MirrorCS"),sQuery(id+"F8.wireOp",EDGE,"E186.MirrorCS")])]})});
            var Q11;
            Q11=makeQuery(id+"F9.boolean.opBoolean","COPY",EDGE,{"derivedFrom":makeQuery(id+"F9.opExtrude","SWEPT_EDGE",EDGE,{"disambiguationData":[OSD([sQuery(id+"F6.wireOp",EDGE,"E159.top"),sQuery(id+"F8.wireOp",EDGE,"E183.MirrorCS"),sQuery(id+"F8.wireOp",EDGE,"E187.MirrorCS")])]})});
            var Q12;
            Q12=makeQuery(id+"F9.boolean.opBoolean","COPY",EDGE,{"derivedFrom":makeQuery(id+"F9.opExtrude","SWEPT_EDGE",EDGE,{"disambiguationData":[OSD([sQuery(id+"F6.wireOp",EDGE,"E159.top"),sQuery(id+"F8.wireOp",EDGE,"E177.MirrorCS"),sQuery(id+"F8.wireOp",EDGE,"E181.MirrorCS")])]})});
            var Q13;
            Q13=makeQuery(id+"F9.boolean.opBoolean","COPY",EDGE,{"derivedFrom":makeQuery(id+"F9.opExtrude","SWEPT_EDGE",EDGE,{"disambiguationData":[OSD([sQuery(id+"F6.wireOp",EDGE,"E159.top"),sQuery(id+"F8.wireOp",EDGE,"E177.MirrorCS"),sQuery(id+"F8.wireOp",EDGE,"E180.MirrorCS")])]})});
            var Q14;
            Q14=makeQuery(id+"F9.boolean.opBoolean","COPY",EDGE,{"derivedFrom":makeQuery(id+"F9.opExtrude","SWEPT_EDGE",EDGE,{"disambiguationData":[OSD([sQuery(id+"F6.wireOp",EDGE,"E159.top"),sQuery(id+"F8.wireOp",EDGE,"E189.MirrorCS"),sQuery(id+"F8.wireOp",EDGE,"E193.MirrorCS")])]})});
            var Q15;
            Q15=makeQuery(id+"F9.boolean.opBoolean","COPY",EDGE,{"derivedFrom":makeQuery(id+"F9.opExtrude","SWEPT_EDGE",EDGE,{"disambiguationData":[OSD([sQuery(id+"F6.wireOp",EDGE,"E159.top"),sQuery(id+"F8.wireOp",EDGE,"E190.MirrorCS"),sQuery(id+"F8.wireOp",EDGE,"E193.MirrorCS")])]})});
            fillet(context, id + "F10", {"entities" : qUnion([Q0, Q1, Q2, Q3, Q4, Q5, Q6, Q7, Q8, Q9, Q10, Q11, Q12, Q13, Q14, Q15]), "radius" : .75 * mm, "tangentPropagation" : true, "allowEdgeOverflow" : false});
        }
        {
            var Q0;
            Q0=makeQuery(id+"F7.opExtrude","SWEPT_EDGE",EDGE,{"disambiguationData":[OSD([sQuery(id+"F6.wireOp",EDGE,"E159.top"),sQuery(id+"F6.wireOp",EDGE,"E159.right")])]});
            var Q1;
            Q1=makeQuery(id+"F7.opExtrude","SWEPT_EDGE",EDGE,{"disambiguationData":[OSD([sQuery(id+"F6.wireOp",EDGE,"E159.top"),sQuery(id+"F6.wireOp",EDGE,"E159.left")])]});
            var Q2;
            Q2=makeQuery(id+"F7.opExtrude","SWEPT_EDGE",EDGE,{"disambiguationData":[OSD([sQuery(id+"F6.wireOp",EDGE,"E159.bottom"),sQuery(id+"F6.wireOp",EDGE,"E159.right")])]});
            var Q3;
            Q3=makeQuery(id+"F7.opExtrude","SWEPT_EDGE",EDGE,{"disambiguationData":[OSD([sQuery(id+"F6.wireOp",EDGE,"E159.bottom"),sQuery(id+"F6.wireOp",EDGE,"E159.left")])]});
            fillet(context, id + "F11", {"entities" : qUnion([Q0, Q1, Q2, Q3]), "radius" : 4 * mm, "tangentPropagation" : true, "allowEdgeOverflow" : false});
        }
        {
            var Q0;
            Q0=qCreatedBy(makeId("Top.planeOp"),FACE);
            var sketch = newSketch(context, id + "F12", { "sketchPlane" : qUnion([Q0])});
            skArc(sketch, "E212", {"start": v(-24.05, -7.66) * mm, "mid": v(-22.46, -10.13) * mm, "end": v(-20.86, -7.66) * mm});
            skArc(sketch, "E213", {"start": v(-20.05, -7.66) * mm, "mid": v(-18.46, -10.13) * mm, "end": v(-16.86, -7.66) * mm});
            skLineSegment(sketch, "E214", {"start": v(-24.05, -7.66) * mm, "end": v(-23.25, -5.88) * mm});
            skLineSegment(sketch, "E215", {"start": v(-20.86, -7.66) * mm, "end": v(-21.67, -5.88) * mm});
            skLineSegment(sketch, "E216", {"start": v(-20.05, -7.66) * mm, "end": v(-19.25, -5.88) * mm});
            skPoint(sketch, "E216.endSnap0", {"position": v(-22.46, -5.88) * mm});
            skLineSegment(sketch, "E217", {"start": v(-16.86, -7.66) * mm, "end": v(-17.67, -5.88) * mm});
            skArc(sketch, "E218.MirrorCS", {"start": v(-20.05, -14.5) * mm, "mid": v(-18.46, -12.03) * mm, "end": v(-16.86, -14.5) * mm});
            skLineSegment(sketch, "E219.MirrorCS", {"start": v(-20.86, -14.5) * mm, "end": v(-21.67, -16.28) * mm});
            skLineSegment(sketch, "E220.MirrorCS", {"start": v(-24.05, -14.5) * mm, "end": v(-23.25, -16.28) * mm});
            skArc(sketch, "E221.MirrorCS", {"start": v(-24.05, -14.5) * mm, "mid": v(-22.46, -12.03) * mm, "end": v(-20.86, -14.5) * mm});
            skPoint(sketch, "E222.MirrorP", {"position": v(-22.46, -16.28) * mm});
            skLineSegment(sketch, "E223.MirrorCS", {"start": v(-20.05, -14.5) * mm, "end": v(-19.25, -16.28) * mm});
            skLineSegment(sketch, "E224.MirrorCS", {"start": v(-16.86, -14.5) * mm, "end": v(-17.67, -16.28) * mm});
            skLineSegment(sketch, "E225.bottom", {"start": v(-25.96, -5.88) * mm, "end": v(-23.25, -5.88) * mm});
            skLineSegment(sketch, "E225.top", {"start": v(-25.96, -16.28) * mm, "end": v(-23.25, -16.28) * mm});
            skLineSegment(sketch, "E225.left", {"start": v(-25.96, -5.88) * mm, "end": v(-25.96, -16.28) * mm});
            skLineSegment(sketch, "E225.right", {"start": v(-14.96, -5.88) * mm, "end": v(-14.96, -16.28) * mm});
            skLineSegment(sketch, "E226.trimOffspring", {"start": v(-17.67, -5.88) * mm, "end": v(-14.96, -5.88) * mm});
            skLineSegment(sketch, "E227.trimOffspring", {"start": v(-17.67, -16.28) * mm, "end": v(-14.96, -16.28) * mm});
            skLineSegment(sketch, "E228.trimOffspring", {"start": v(-21.67, -16.28) * mm, "end": v(-19.25, -16.28) * mm});
            skLineSegment(sketch, "E229.trimOffspring", {"start": v(-21.67, -5.88) * mm, "end": v(-19.25, -5.88) * mm});
            skSolve(sketch);
        }
        {
            var Q0;
            Q0=makeQuery(id+"F12.imprint","IMPRINT",FACE,{"disambiguationData":[TD([[makeQuery(id+"F12.imprint","IMPRINT",EDGE,{"derivedFrom":sQuery(id+"F12.wireOp",EDGE,"E212")}),-1.0]])]});
            var Q1;
            Q1=makeQuery(id+"F1.opExtrude","CAP_FACE",FACE,{"disambiguationData":[OSD([sQuery(id+"F0.wireOp",EDGE,"E0.bottom"),sQuery(id+"F0.wireOp",EDGE,"E0.top"),sQuery(id+"F0.wireOp",EDGE,"E0.left"),sQuery(id+"F0.wireOp",EDGE,"E0.right")])],"isStart":false});
            extrude(context, id + "F13", {"entities" : qUnion([Q0]), "endBound" : BoundingType.UP_TO_SURFACE, "endBoundEntityFace" : qUnion([Q1]), "depth" : 25 * mm});
        }
        {
            var Q0;
            Q0=makeQuery(id+"F13.opExtrude","SWEPT_EDGE",EDGE,{"disambiguationData":[OSD([sQuery(id+"F12.wireOp",EDGE,"E225.bottom"),sQuery(id+"F12.wireOp",EDGE,"E225.left")])]});
            var Q1;
            Q1=makeQuery(id+"F13.opExtrude","SWEPT_EDGE",EDGE,{"disambiguationData":[OSD([sQuery(id+"F12.wireOp",EDGE,"E225.top"),sQuery(id+"F12.wireOp",EDGE,"E225.left")])]});
            var Q2;
            Q2=makeQuery(id+"F13.opExtrude","SWEPT_EDGE",EDGE,{"disambiguationData":[OSD([sQuery(id+"F12.wireOp",EDGE,"E225.right"),sQuery(id+"F12.wireOp",EDGE,"E227.trimOffspring")])]});
            var Q3;
            Q3=makeQuery(id+"F13.opExtrude","SWEPT_EDGE",EDGE,{"disambiguationData":[OSD([sQuery(id+"F12.wireOp",EDGE,"E225.right"),sQuery(id+"F12.wireOp",EDGE,"E226.trimOffspring")])]});
            fillet(context, id + "F14", {"entities" : qUnion([Q0, Q1, Q2, Q3]), "radius" : 2 * mm, "tangentPropagation" : true, "allowEdgeOverflow" : false});
        }
        {
            var Q0;
            Q0=makeQuery(id+"F13.opExtrude","SWEPT_EDGE",EDGE,{"disambiguationData":[OSD([sQuery(id+"F12.wireOp",EDGE,"E220.MirrorCS"),sQuery(id+"F12.wireOp",EDGE,"E225.top")])]});
            var Q1;
            Q1=makeQuery(id+"F13.opExtrude","SWEPT_EDGE",EDGE,{"disambiguationData":[OSD([sQuery(id+"F12.wireOp",EDGE,"E219.MirrorCS"),sQuery(id+"F12.wireOp",EDGE,"E228.trimOffspring")])]});
            var Q2;
            Q2=makeQuery(id+"F13.opExtrude","SWEPT_EDGE",EDGE,{"disambiguationData":[OSD([sQuery(id+"F12.wireOp",EDGE,"E223.MirrorCS"),sQuery(id+"F12.wireOp",EDGE,"E228.trimOffspring")])]});
            var Q3;
            Q3=makeQuery(id+"F13.opExtrude","SWEPT_EDGE",EDGE,{"disambiguationData":[OSD([sQuery(id+"F12.wireOp",EDGE,"E224.MirrorCS"),sQuery(id+"F12.wireOp",EDGE,"E227.trimOffspring")])]});
            var Q4;
            Q4=makeQuery(id+"F13.opExtrude","SWEPT_EDGE",EDGE,{"disambiguationData":[OSD([sQuery(id+"F12.wireOp",EDGE,"E217"),sQuery(id+"F12.wireOp",EDGE,"E226.trimOffspring")])]});
            var Q5;
            Q5=makeQuery(id+"F13.opExtrude","SWEPT_EDGE",EDGE,{"disambiguationData":[OSD([sQuery(id+"F12.wireOp",EDGE,"E216"),sQuery(id+"F12.wireOp",EDGE,"E229.trimOffspring")])]});
            var Q6;
            Q6=makeQuery(id+"F13.opExtrude","SWEPT_EDGE",EDGE,{"disambiguationData":[OSD([sQuery(id+"F12.wireOp",EDGE,"E215"),sQuery(id+"F12.wireOp",EDGE,"E229.trimOffspring")])]});
            var Q7;
            Q7=makeQuery(id+"F13.opExtrude","SWEPT_EDGE",EDGE,{"disambiguationData":[OSD([sQuery(id+"F12.wireOp",EDGE,"E214"),sQuery(id+"F12.wireOp",EDGE,"E225.bottom")])]});
            fillet(context, id + "F15", {"entities" : qUnion([Q0, Q1, Q2, Q3, Q4, Q5, Q6, Q7]), "radius" : .75 * mm, "tangentPropagation" : true, "allowEdgeOverflow" : false});
        }
        {
            var Q0;
            Q0=makeQuery(id+"F2.imprint","IMPRINT",FACE,{"disambiguationData":[TD([[makeQuery(id+"F2.imprint","IMPRINT",EDGE,{"derivedFrom":sQuery(id+"F2.wireOp",EDGE,"E99")}),-1.0]])]});
            extrude(context, id + "F16", {"entities" : qUnion([Q0]), "oppositeDirection" : true, "depth" : 2.75 * mm});
        }
        {
            var Q0;
            Q0=makeQuery(id+"F16.opExtrude","SWEPT_EDGE",EDGE,{"disambiguationData":[OSD([sQuery(id+"F2.wireOp",EDGE,"E123.bottom"),sQuery(id+"F2.wireOp",EDGE,"E123.left")])]});
            var Q1;
            Q1=makeQuery(id+"F16.opExtrude","SWEPT_EDGE",EDGE,{"disambiguationData":[OSD([sQuery(id+"F2.wireOp",EDGE,"E156"),sQuery(id+"F2.wireOp",EDGE,"E158")])]});
            var Q2;
            Q2=makeQuery(id+"F16.opExtrude","SWEPT_EDGE",EDGE,{"disambiguationData":[OSD([sQuery(id+"F2.wireOp",EDGE,"E156"),sQuery(id+"F2.wireOp",EDGE,"E157")])]});
            var Q3;
            Q3=makeQuery(id+"F16.opExtrude","SWEPT_EDGE",EDGE,{"disambiguationData":[OSD([sQuery(id+"F2.wireOp",EDGE,"E123.top"),sQuery(id+"F2.wireOp",EDGE,"E123.left")])]});
            fillet(context, id + "F17", {"entities" : qUnion([Q0, Q1, Q2, Q3]), "radius" : 2 * mm, "tangentPropagation" : true, "allowEdgeOverflow" : false});
        }
        {
            var Q0;
            Q0=makeQuery(id+"F16.opExtrude","SWEPT_EDGE",EDGE,{"disambiguationData":[OSD([sQuery(id+"F2.wireOp",EDGE,"E103"),sQuery(id+"F2.wireOp",EDGE,"E123.bottom")])]});
            var Q1;
            Q1=makeQuery(id+"F16.opExtrude","SWEPT_EDGE",EDGE,{"disambiguationData":[OSD([sQuery(id+"F2.wireOp",EDGE,"E100"),sQuery(id+"F2.wireOp",EDGE,"E129.trimOffspring")])]});
            var Q2;
            Q2=makeQuery(id+"F16.opExtrude","SWEPT_EDGE",EDGE,{"disambiguationData":[OSD([sQuery(id+"F2.wireOp",EDGE,"E122.MirrorCS"),sQuery(id+"F2.wireOp",EDGE,"E129.trimOffspring")])]});
            var Q3;
            Q3=makeQuery(id+"F16.opExtrude","SWEPT_EDGE",EDGE,{"disambiguationData":[OSD([sQuery(id+"F2.wireOp",EDGE,"E119.MirrorCS"),sQuery(id+"F2.wireOp",EDGE,"E128.trimOffspring")])]});
            var Q4;
            Q4=makeQuery(id+"F16.opExtrude","SWEPT_EDGE",EDGE,{"disambiguationData":[OSD([sQuery(id+"F2.wireOp",EDGE,"E120.MirrorCS"),sQuery(id+"F2.wireOp",EDGE,"E128.trimOffspring")])]});
            var Q5;
            Q5=makeQuery(id+"F16.opExtrude","SWEPT_EDGE",EDGE,{"disambiguationData":[OSD([sQuery(id+"F2.wireOp",EDGE,"E115.MirrorCS"),sQuery(id+"F2.wireOp",EDGE,"E127.trimOffspring")])]});
            var Q6;
            Q6=makeQuery(id+"F16.opExtrude","SWEPT_EDGE",EDGE,{"disambiguationData":[OSD([sQuery(id+"F2.wireOp",EDGE,"E114.MirrorCS"),sQuery(id+"F2.wireOp",EDGE,"E127.trimOffspring")])]});
            var Q7;
            Q7=makeQuery(id+"F16.opExtrude","SWEPT_EDGE",EDGE,{"disambiguationData":[OSD([sQuery(id+"F2.wireOp",EDGE,"E118.MirrorCS"),sQuery(id+"F2.wireOp",EDGE,"E130")])]});
            var Q8;
            Q8=makeQuery(id+"F16.opExtrude","SWEPT_EDGE",EDGE,{"disambiguationData":[OSD([sQuery(id+"F2.wireOp",EDGE,"E145.MirrorCS"),sQuery(id+"F2.wireOp",EDGE,"E154")])]});
            var Q9;
            Q9=makeQuery(id+"F16.opExtrude","SWEPT_EDGE",EDGE,{"disambiguationData":[OSD([sQuery(id+"F2.wireOp",EDGE,"E133.MirrorCS"),sQuery(id+"F2.wireOp",EDGE,"E137.MirrorCS")])]});
            var Q10;
            Q10=makeQuery(id+"F16.opExtrude","SWEPT_EDGE",EDGE,{"disambiguationData":[OSD([sQuery(id+"F2.wireOp",EDGE,"E135.MirrorCS"),sQuery(id+"F2.wireOp",EDGE,"E137.MirrorCS")])]});
            var Q11;
            Q11=makeQuery(id+"F16.opExtrude","SWEPT_EDGE",EDGE,{"disambiguationData":[OSD([sQuery(id+"F2.wireOp",EDGE,"E132.MirrorCS"),sQuery(id+"F2.wireOp",EDGE,"E150.MirrorCS")])]});
            var Q12;
            Q12=makeQuery(id+"F16.opExtrude","SWEPT_EDGE",EDGE,{"disambiguationData":[OSD([sQuery(id+"F2.wireOp",EDGE,"E132.MirrorCS"),sQuery(id+"F2.wireOp",EDGE,"E151.MirrorCS")])]});
            var Q13;
            Q13=makeQuery(id+"F16.opExtrude","SWEPT_EDGE",EDGE,{"disambiguationData":[OSD([sQuery(id+"F2.wireOp",EDGE,"E142.MirrorCS"),sQuery(id+"F2.wireOp",EDGE,"E158")])]});
            var Q14;
            Q14=makeQuery(id+"F16.opExtrude","SWEPT_EDGE",EDGE,{"disambiguationData":[OSD([sQuery(id+"F2.wireOp",EDGE,"E147.MirrorCS"),sQuery(id+"F2.wireOp",EDGE,"E157")])]});
            var Q15;
            Q15=makeQuery(id+"F16.opExtrude","SWEPT_EDGE",EDGE,{"disambiguationData":[OSD([sQuery(id+"F2.wireOp",EDGE,"E136.MirrorCS"),sQuery(id+"F2.wireOp",EDGE,"E153.MirrorCS")])]});
            var Q16;
            Q16=makeQuery(id+"F16.opExtrude","SWEPT_EDGE",EDGE,{"disambiguationData":[OSD([sQuery(id+"F2.wireOp",EDGE,"E136.MirrorCS"),sQuery(id+"F2.wireOp",EDGE,"E143.MirrorCS")])]});
            var Q17;
            Q17=makeQuery(id+"F16.opExtrude","SWEPT_EDGE",EDGE,{"disambiguationData":[OSD([sQuery(id+"F2.wireOp",EDGE,"E134.MirrorCS"),sQuery(id+"F2.wireOp",EDGE,"E146.MirrorCS")])]});
            var Q18;
            Q18=makeQuery(id+"F16.opExtrude","SWEPT_EDGE",EDGE,{"disambiguationData":[OSD([sQuery(id+"F2.wireOp",EDGE,"E144.MirrorCS"),sQuery(id+"F2.wireOp",EDGE,"E146.MirrorCS")])]});
            var Q19;
            Q19=makeQuery(id+"F16.opExtrude","SWEPT_EDGE",EDGE,{"disambiguationData":[OSD([sQuery(id+"F2.wireOp",EDGE,"E152.MirrorCS"),sQuery(id+"F2.wireOp",EDGE,"E155")])]});
            var Q20;
            Q20=makeQuery(id+"F16.opExtrude","SWEPT_EDGE",EDGE,{"disambiguationData":[OSD([sQuery(id+"F2.wireOp",EDGE,"E117.MirrorCS"),sQuery(id+"F2.wireOp",EDGE,"E131")])]});
            var Q21;
            Q21=makeQuery(id+"F16.opExtrude","SWEPT_EDGE",EDGE,{"disambiguationData":[OSD([sQuery(id+"F2.wireOp",EDGE,"E121.MirrorCS"),sQuery(id+"F2.wireOp",EDGE,"E126.trimOffspring")])]});
            var Q22;
            Q22=makeQuery(id+"F16.opExtrude","SWEPT_EDGE",EDGE,{"disambiguationData":[OSD([sQuery(id+"F2.wireOp",EDGE,"E110.MirrorCS"),sQuery(id+"F2.wireOp",EDGE,"E126.trimOffspring")])]});
            var Q23;
            Q23=makeQuery(id+"F16.opExtrude","SWEPT_EDGE",EDGE,{"disambiguationData":[OSD([sQuery(id+"F2.wireOp",EDGE,"E106.MirrorCS"),sQuery(id+"F2.wireOp",EDGE,"E125.trimOffspring")])]});
            var Q24;
            Q24=makeQuery(id+"F16.opExtrude","SWEPT_EDGE",EDGE,{"disambiguationData":[OSD([sQuery(id+"F2.wireOp",EDGE,"E111.MirrorCS"),sQuery(id+"F2.wireOp",EDGE,"E125.trimOffspring")])]});
            var Q25;
            Q25=makeQuery(id+"F16.opExtrude","SWEPT_EDGE",EDGE,{"disambiguationData":[OSD([sQuery(id+"F2.wireOp",EDGE,"E116.MirrorCS"),sQuery(id+"F2.wireOp",EDGE,"E124.trimOffspring")])]});
            var Q26;
            Q26=makeQuery(id+"F16.opExtrude","SWEPT_EDGE",EDGE,{"disambiguationData":[OSD([sQuery(id+"F2.wireOp",EDGE,"E102.MirrorCS"),sQuery(id+"F2.wireOp",EDGE,"E124.trimOffspring")])]});
            var Q27;
            Q27=makeQuery(id+"F16.opExtrude","SWEPT_EDGE",EDGE,{"disambiguationData":[OSD([sQuery(id+"F2.wireOp",EDGE,"E104"),sQuery(id+"F2.wireOp",EDGE,"E123.top")])]});
            fillet(context, id + "F18", {"entities" : qUnion([Q0, Q1, Q2, Q3, Q4, Q5, Q6, Q7, Q8, Q9, Q10, Q11, Q12, Q13, Q14, Q15, Q16, Q17, Q18, Q19, Q20, Q21, Q22, Q23, Q24, Q25, Q26, Q27]), "radius" : .75 * mm, "tangentPropagation" : true, "allowEdgeOverflow" : false});
        }
    });
